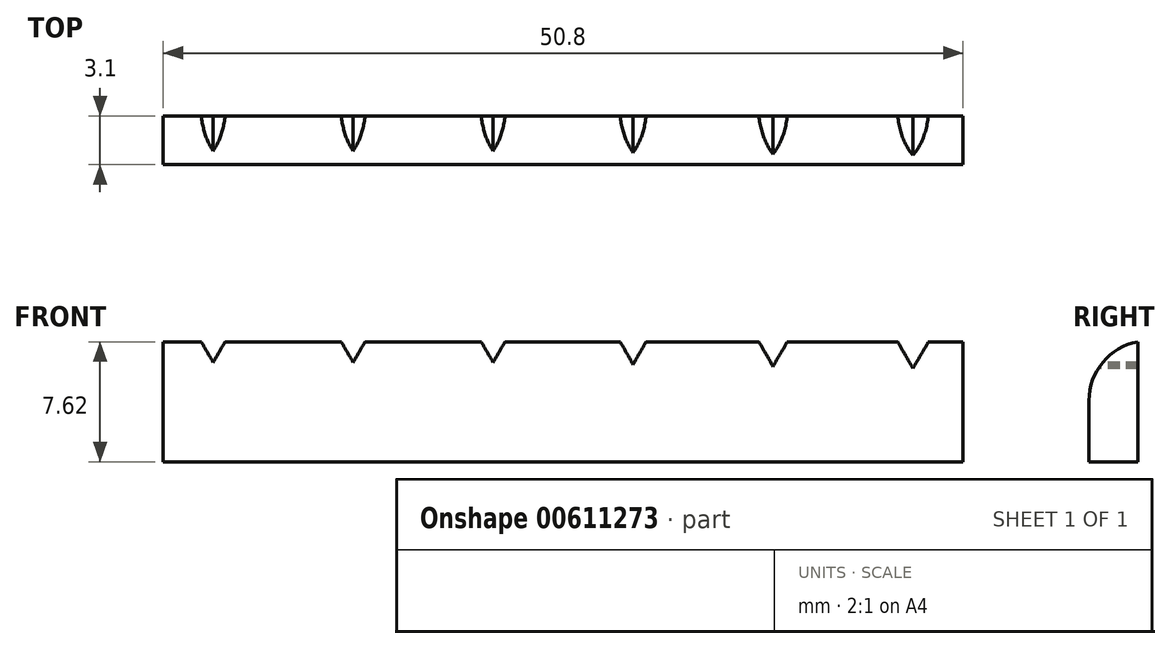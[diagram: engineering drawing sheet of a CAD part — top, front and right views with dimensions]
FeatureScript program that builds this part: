
annotation { "Feature Type Name" : "Feature", "Feature Type Description" : "" }
export const myFeature = defineFeature(function(context is Context, id is Id, definition is map)
    precondition{}
    {
        {
            var Q0;
            Q0=qCreatedBy(makeId("Top.planeOp"),FACE);
            var sketch = newSketch(context, id + "F0", { "sketchPlane" : qUnion([Q0])});
            skLineSegment(sketch, "E0.bottom", {"start": v(-25.4, 0) * mm, "end": v(25.4, 0) * mm});
            skLineSegment(sketch, "E0.top", {"start": v(-25.4, 3.1) * mm, "end": v(25.4, 3.1) * mm});
            skLineSegment(sketch, "E0.left", {"start": v(-25.4, 0) * mm, "end": v(-25.4, 3.1) * mm});
            skLineSegment(sketch, "E0.right", {"start": v(25.4, 0) * mm, "end": v(25.4, 3.1) * mm});
            skSolve(sketch);
        }
        {
            var Q0;
            Q0=makeQuery(id+"F0.imprint","IMPRINT",FACE,{"disambiguationData":[TD([[makeQuery(id+"F0.imprint","IMPRINT",EDGE,{"derivedFrom":sQuery(id+"F0.wireOp",EDGE,"E0.bottom")}),1.0]])]});
            extrude(context, id + "F1", {"entities" : qUnion([Q0]), "depth" : 7.62 * mm, "offsetDistance" : 25.4 * mm});
        }
        {
            var Q0;
            Q0=makeQuery(id+"F1.opExtrude","SWEPT_FACE",FACE,{"disambiguationData":[OSD([sQuery(id+"F0.wireOp",EDGE,"E0.bottom")])]});
            var sketch = newSketch(context, id + "F2", { "sketchPlane" : qUnion([Q0])});
            skCircle(sketch, "E1.cCircle", {"center": v(-22.23, 7.78) * mm, "radius": 0.73 * mm, "construction": true});
            skLineSegment(sketch, "E1.0", {"start": v(-20.96, 8.5) * mm, "end": v(-22.23, 6.3) * mm});
            skLineSegment(sketch, "E1.1", {"start": v(-22.23, 6.3) * mm, "end": v(-23.5, 8.5) * mm});
            skLineSegment(sketch, "E1.2", {"start": v(-23.5, 8.5) * mm, "end": v(-20.96, 8.5) * mm});
            skPoint(sketch, "E1.0.midPoint", {"position": v(-21.6, 7.4) * mm});
            skCircle(sketch, "E2.cCircle", {"center": v(-13.34, 7.78) * mm, "radius": 0.73 * mm, "construction": true});
            skLineSegment(sketch, "E2.0", {"start": v(-12.06, 8.5) * mm, "end": v(-13.34, 6.3) * mm});
            skLineSegment(sketch, "E2.1", {"start": v(-13.34, 6.3) * mm, "end": v(-14.6, 8.5) * mm});
            skLineSegment(sketch, "E2.2", {"start": v(-14.6, 8.5) * mm, "end": v(-12.07, 8.5) * mm});
            skPoint(sketch, "E2.0.midPoint", {"position": v(-12.7, 7.4) * mm});
            skCircle(sketch, "E3.cCircle", {"center": v(22.22, 7.4) * mm, "radius": 0.73 * mm, "construction": true});
            skLineSegment(sketch, "E3.0", {"start": v(23.5, 8.13) * mm, "end": v(22.22, 5.93) * mm});
            skLineSegment(sketch, "E3.1", {"start": v(22.22, 5.93) * mm, "end": v(20.95, 8.13) * mm});
            skLineSegment(sketch, "E3.2", {"start": v(20.96, 8.13) * mm, "end": v(23.5, 8.13) * mm});
            skPoint(sketch, "E3.0.midPoint", {"position": v(22.86, 7.03) * mm});
            skCircle(sketch, "E4.cCircle", {"center": v(13.33, 7.52) * mm, "radius": 0.73 * mm, "construction": true});
            skLineSegment(sketch, "E4.0", {"start": v(14.6, 8.26) * mm, "end": v(13.33, 6.06) * mm});
            skLineSegment(sketch, "E4.1", {"start": v(13.34, 6.06) * mm, "end": v(12.06, 8.26) * mm});
            skLineSegment(sketch, "E4.2", {"start": v(12.06, 8.26) * mm, "end": v(14.6, 8.26) * mm});
            skPoint(sketch, "E4.0.midPoint", {"position": v(13.97, 7.16) * mm});
            skLineSegment(sketch, "E5.0", {"start": v(-3.18, 8.5) * mm, "end": v(-4.45, 6.3) * mm});
            skLineSegment(sketch, "E5.1", {"start": v(-4.45, 6.3) * mm, "end": v(-5.72, 8.5) * mm});
            skLineSegment(sketch, "E5.2", {"start": v(-5.72, 8.5) * mm, "end": v(-3.18, 8.5) * mm});
            skLineSegment(sketch, "E6.0", {"start": v(5.72, 8.38) * mm, "end": v(4.45, 6.18) * mm});
            skLineSegment(sketch, "E6.1", {"start": v(4.45, 6.18) * mm, "end": v(3.18, 8.38) * mm});
            skLineSegment(sketch, "E6.2", {"start": v(3.18, 8.38) * mm, "end": v(5.72, 8.38) * mm});
            skSolve(sketch);
        }
        {
            var Q0;
            Q0=makeQuery(id+"F1.opExtrude","CAP_EDGE",EDGE,{"disambiguationData":[OSD([sQuery(id+"F0.wireOp",EDGE,"E0.bottom")])],"isStart":false});
            fillet(context, id + "F3", {"entities" : qUnion([Q0]), "radius" : 3.8 * mm, "tangentPropagation" : true, "allowEdgeOverflow" : false});
        }
        {
            var Q0;
            {var subQ0=sQuery(id+"F2.wireOp",EDGE,"E1.1");var subQ1=sQuery(id+"F2.wireOp",EDGE,"E1.0");var subQ2=makeQuery(id+"F2.imprint","INTERSECT",VERTEX,{"derivedFrom":[subQ1,subQ0]});Q0=makeQuery(id+"F2.imprint","IMPRINT",FACE,{"disambiguationData":[TD([[makeQuery(id+"F2.imprint","IMPRINT",EDGE,{"disambiguationData":[TD([[subQ2,1.0]])],"derivedFrom":subQ1}),-1.0]])]});}
            var Q1;
            {var subQ0=sQuery(id+"F2.wireOp",EDGE,"E2.1");var subQ1=sQuery(id+"F2.wireOp",EDGE,"E2.0");var subQ2=makeQuery(id+"F2.imprint","INTERSECT",VERTEX,{"derivedFrom":[subQ1,subQ0]});Q1=makeQuery(id+"F2.imprint","IMPRINT",FACE,{"disambiguationData":[TD([[makeQuery(id+"F2.imprint","IMPRINT",EDGE,{"disambiguationData":[TD([[subQ2,1.0]])],"derivedFrom":subQ1}),-1.0]])]});}
            var Q2;
            {var subQ0=sQuery(id+"F2.wireOp",EDGE,"E4.1");var subQ1=sQuery(id+"F2.wireOp",EDGE,"E4.0");var subQ2=makeQuery(id+"F2.imprint","INTERSECT",VERTEX,{"derivedFrom":[subQ1,subQ0]});Q2=makeQuery(id+"F2.imprint","IMPRINT",FACE,{"disambiguationData":[TD([[makeQuery(id+"F2.imprint","IMPRINT",EDGE,{"disambiguationData":[TD([[subQ2,1.0]])],"derivedFrom":subQ1}),-1.0]])]});}
            var Q3;
            {var subQ0=sQuery(id+"F2.wireOp",EDGE,"E3.1");var subQ1=sQuery(id+"F2.wireOp",EDGE,"E3.0");var subQ2=makeQuery(id+"F2.imprint","INTERSECT",VERTEX,{"derivedFrom":[subQ1,subQ0]});Q3=makeQuery(id+"F2.imprint","IMPRINT",FACE,{"disambiguationData":[TD([[makeQuery(id+"F2.imprint","IMPRINT",EDGE,{"disambiguationData":[TD([[subQ2,1.0]])],"derivedFrom":subQ1}),-1.0]])]});}
            var Q4;
            {var subQ0=sQuery(id+"F2.wireOp",EDGE,"E5.1");var subQ1=sQuery(id+"F2.wireOp",EDGE,"E5.0");var subQ2=makeQuery(id+"F2.imprint","INTERSECT",VERTEX,{"derivedFrom":[subQ1,subQ0]});Q4=makeQuery(id+"F2.imprint","IMPRINT",FACE,{"disambiguationData":[TD([[makeQuery(id+"F2.imprint","IMPRINT",EDGE,{"disambiguationData":[TD([[subQ2,1.0]])],"derivedFrom":subQ1}),-1.0]])]});}
            var Q5;
            {var subQ0=sQuery(id+"F2.wireOp",EDGE,"E6.1");var subQ1=sQuery(id+"F2.wireOp",EDGE,"E6.0");var subQ2=makeQuery(id+"F2.imprint","INTERSECT",VERTEX,{"derivedFrom":[subQ1,subQ0]});Q5=makeQuery(id+"F2.imprint","IMPRINT",FACE,{"disambiguationData":[TD([[makeQuery(id+"F2.imprint","IMPRINT",EDGE,{"disambiguationData":[TD([[subQ2,1.0]])],"derivedFrom":subQ1}),-1.0]])]});}
            extrude(context, id + "F4", {"entities" : qUnion([Q0, Q1, Q2, Q3, Q4, Q5]), "operationType" : NewBodyOperationType.REMOVE, "oppositeDirection" : true, "depth" : 25.4 * mm, "offsetDistance" : 25.4 * mm});
        }
    });
